# Revit family: Воздухонагреватель электрический прямоугольный E
name_source: partatom
category: Оборудование
units: mm (PartAtom-declared; Revit-internal decimal feet)

## family parameters
Всегда вертикально = Да
Заголовок OmniClass = Climate Control (HVAC)
На основе рабочей плоскости = Нет
Номер OmniClass = 23.75.00.00
Общий = Нет
При загрузке вырезать с полостями = Нет
Размер круглого соединителя = Использовать диаметр
Тип детали = Нормальный
Точка расчета площади = Нет

## types (8) — shared parameters
ADSK_Единица измерения = шт.
ADSK_Завод-изготовитель = Naveka
ADSK_Наименование = Воздухонагреватель электрический для прямоугольного канала E
Материал = RAL 0000 Серый металл
Напряжение U,В = 3-380
Таблица = Электронагреватель Е

## per-type parameters (varying)
| type | ADSK_Марка | B | B1 | B3 | H | H1 | H3 | L | L1 | s | Масса, кг | Мощность нагревателя N,кВт | Ток, А | Требуемая мощность, кВт |
| E...-5025 | E13,5-5025 | 500 мм | 520 мм | 625 мм | 250 мм | 270 мм | 254 мм | 500 мм | 430 мм | 20 мм | 9,4 | 13,5 | 20,5 | 14 мм |
| E...-5030 | E21-5030 | 500 мм | 520 мм | 655 мм | 300 мм | 320 мм | 304 мм | 500 мм | 430 мм | 20 мм | 11,8 | 21 | 31,9 | 21 мм |
| E...-6030 | E15-6030 | 600 мм | 620 мм | 725 мм | 300 мм | 320 мм | 304 мм | 500 мм | 430 мм | 20 мм | 11 | 15 | 22,8 | 15 мм |
| E...-6035 | E37,5-6035 | 600 мм | 620 мм | 725 мм | 350 мм | 370 мм | 354 мм | 500 мм | 430 мм | 20 мм | 17,4 | 37,5 | 57 | 38 мм |
| E...-7040 | E97,5-7040 | 700 мм | 730 мм | 825 мм | 400 мм | 430 мм | 404 мм | 600 мм | 530 мм | 30 мм | 31,9 | 97,5 | 148 | 98 мм |
| E...-8050 | E97,5-8050 | 800 мм | 830 мм | 925 мм | 500 мм | 530 мм | 504 мм | 500 мм | 430 мм | 30 мм | 34 | 97,5 | 148 | 98 мм |
| E...-10050 | E97,5-10050 | 1000 мм | 1030 мм | 1125 мм | 500 мм | 530 мм | 504 мм | 500 мм | 430 мм | 30 мм | 35,9 | 97,5 | 148 | 98 мм |
| E...-4020 | E6-4020 | 400 мм | 420 мм | 525 мм | 200 мм | 220 мм | 204 мм | 500 мм | 430 мм | 20 мм | 6,3 | 6 | 9,2 | 6 мм |
